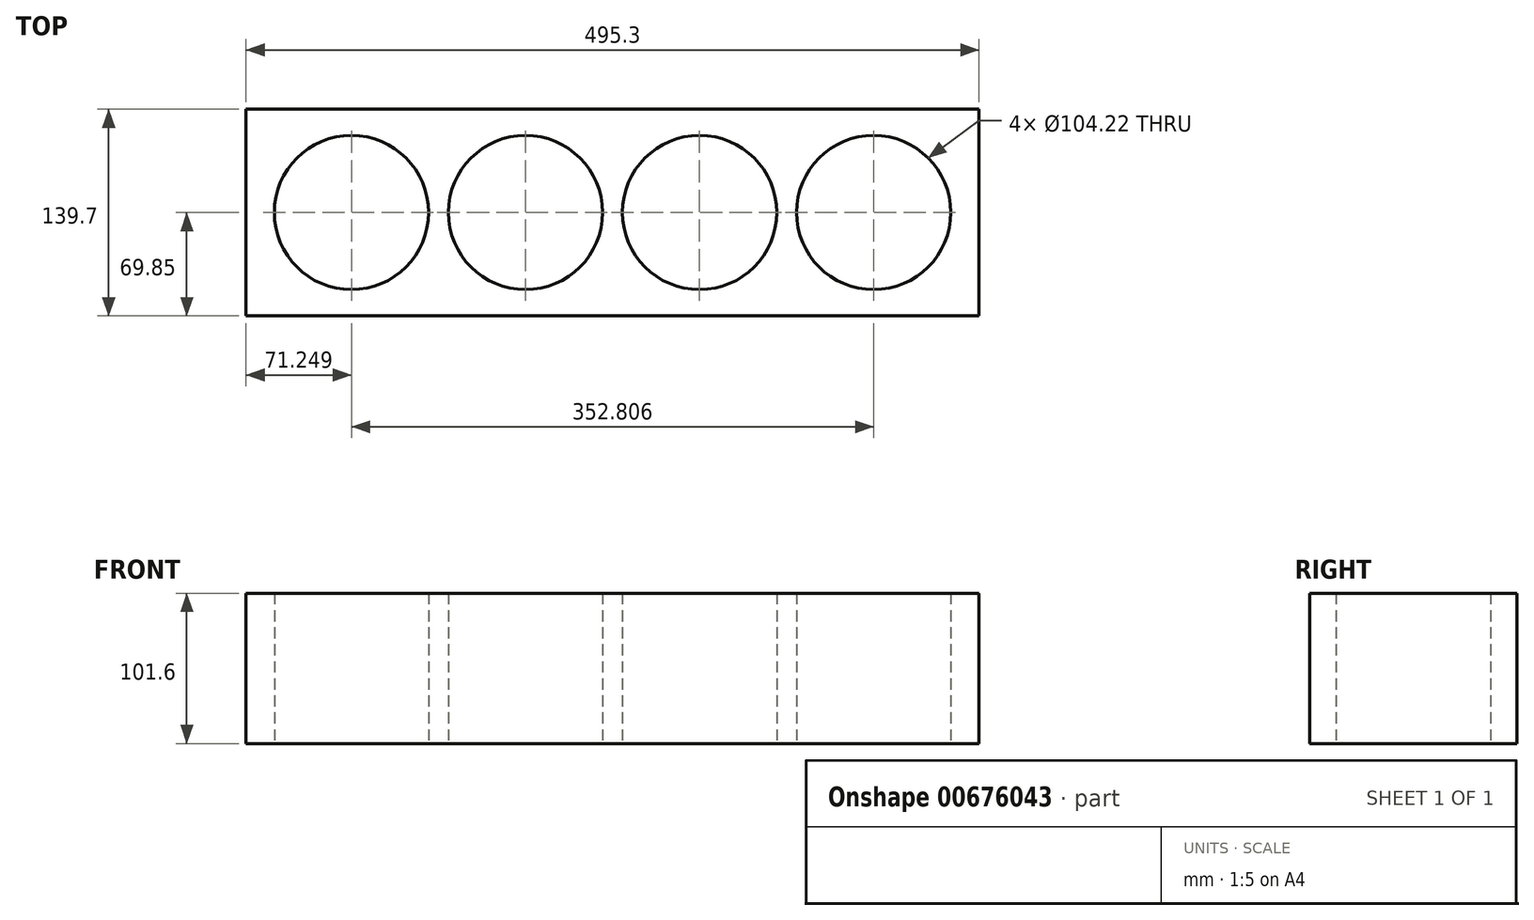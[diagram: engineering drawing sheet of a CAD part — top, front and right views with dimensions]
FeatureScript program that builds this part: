
annotation { "Feature Type Name" : "Feature", "Feature Type Description" : "" }
export const myFeature = defineFeature(function(context is Context, id is Id, definition is map)
    precondition{}
    {
        {
            var Q0;
            Q0=qCreatedBy(makeId("Top.planeOp"),FACE);
            var sketch = newSketch(context, id + "F0", { "sketchPlane" : qUnion([Q0])});
            skCircle(sketch, "E0", {"center": v(-161.23, 0) * mm, "radius": 52.1 * mm});
            skCircle(sketch, "E1.1.0.0", {"center": v(-43.63, 0) * mm, "radius": 52.1 * mm});
            skCircle(sketch, "E1.2.0.0", {"center": v(73.97, 0) * mm, "radius": 52.1 * mm});
            skCircle(sketch, "E1.3.0.0", {"center": v(191.58, 0) * mm, "radius": 52.1 * mm});
            skLineSegment(sketch, "E1.direction1", {"start": v(-161.23, 0) * mm, "end": v(-43.63, 0) * mm, "construction": true});
            skLineSegment(sketch, "E2", {"start": v(-161.23, 0) * mm, "end": v(191.58, 0) * mm, "construction": true});
            skLineSegment(sketch, "E3.bottom", {"start": v(262.82, 69.85) * mm, "end": v(-232.48, 69.85) * mm});
            skLineSegment(sketch, "E3.top", {"start": v(262.82, -69.85) * mm, "end": v(-232.48, -69.85) * mm});
            skLineSegment(sketch, "E3.left", {"start": v(262.82, 69.85) * mm, "end": v(262.82, -69.85) * mm});
            skLineSegment(sketch, "E3.right", {"start": v(-232.48, 69.85) * mm, "end": v(-232.48, -69.85) * mm});
            skPoint(sketch, "E3.middle", {"position": v(15.17, 0) * mm});
            skSolve(sketch);
        }
        {
            var Q0;
            Q0=makeQuery(id+"F0.imprint","IMPRINT",FACE,{"disambiguationData":[TD([[makeQuery(id+"F0.imprint","IMPRINT",EDGE,{"derivedFrom":sQuery(id+"F0.wireOp",EDGE,"E0")}),-1.0]])]});
            extrude(context, id + "F1", {"entities" : qUnion([Q0]), "depth" : 101.6 * mm, "offsetDistance" : 25.4 * mm});
        }
    });
